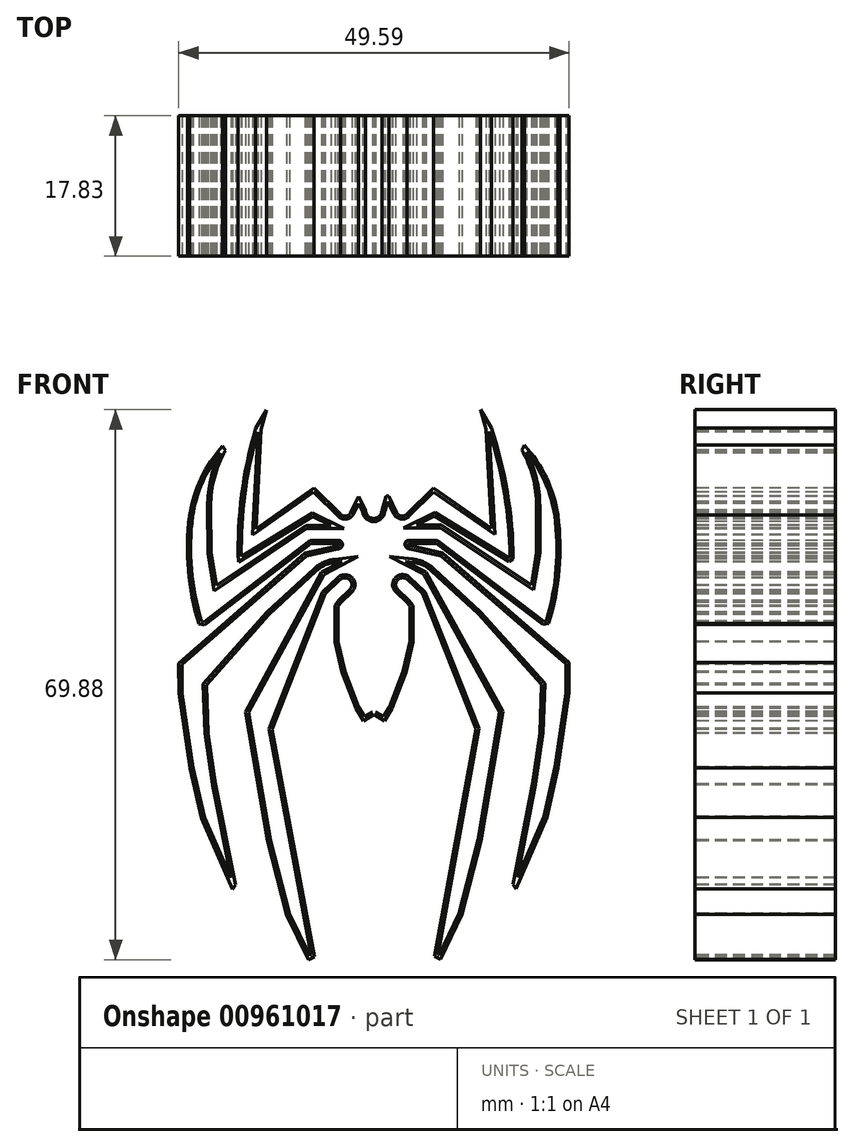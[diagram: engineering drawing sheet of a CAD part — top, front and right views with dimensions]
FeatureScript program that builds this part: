
annotation { "Feature Type Name" : "Feature", "Feature Type Description" : "" }
export const myFeature = defineFeature(function(context is Context, id is Id, definition is map)
    precondition{}
    {
        {
            var Q0;
            Q0=qCreatedBy(makeId("Front.planeOp"),FACE);
            var sketch = newSketch(context, id + "F0", { "sketchPlane" : qUnion([Q0])});
            skArc(sketch, "E0", {"start": v(10.3, 43.39) * mm, "mid": v(11.32, 42.32) * mm, "end": v(12.36, 43.36) * mm});
            skLineSegment(sketch, "E1", {"start": v(12.36, 43.36) * mm, "end": v(12.91, 45.08) * mm});
            skLineSegment(sketch, "E2", {"start": v(10.3, 43.39) * mm, "end": v(9.41, 45.08) * mm});
            skArc(sketch, "E3", {"start": v(13.25, 45.08) * mm, "mid": v(13.08, 45.2) * mm, "end": v(12.91, 45.08) * mm});
            skLineSegment(sketch, "E4", {"start": v(13.25, 45.08) * mm, "end": v(14.26, 43.06) * mm});
            skArc(sketch, "E5", {"start": v(14.26, 43.06) * mm, "mid": v(14.86, 42.62) * mm, "end": v(15.56, 42.87) * mm});
            skLineSegment(sketch, "E6", {"start": v(15.56, 42.87) * mm, "end": v(18.91, 46.2) * mm});
            skLineSegment(sketch, "E7", {"start": v(18.91, 46.2) * mm, "end": v(26.28, 41.06) * mm});
            skLineSegment(sketch, "E8", {"start": v(26.28, 41.06) * mm, "end": v(25.6, 53.69) * mm});
            skLineSegment(sketch, "E9", {"start": v(25.6, 53.69) * mm, "end": v(24.88, 56.14) * mm});
            skLineSegment(sketch, "E10", {"start": v(24.88, 56.14) * mm, "end": v(26.28, 53.79) * mm});
            skArc(sketch, "E11", {"start": v(29.06, 37.18) * mm, "mid": v(28.32, 45.6) * mm, "end": v(26.28, 53.79) * mm});
            skLineSegment(sketch, "E12", {"start": v(29.06, 37.18) * mm, "end": v(28.54, 36.84) * mm});
            skLineSegment(sketch, "E13", {"start": v(28.54, 36.84) * mm, "end": v(19.08, 42.61) * mm});
            skLineSegment(sketch, "E14", {"start": v(19.08, 42.61) * mm, "end": v(16.77, 41.46) * mm});
            skLineSegment(sketch, "E15", {"start": v(16.77, 41.46) * mm, "end": v(19.96, 41.46) * mm});
            skLineSegment(sketch, "E16", {"start": v(19.96, 41.46) * mm, "end": v(31.36, 33.86) * mm});
            skLineSegment(sketch, "E17", {"start": v(31.36, 33.86) * mm, "end": v(32.04, 38) * mm});
            skLineSegment(sketch, "E18", {"start": v(32.04, 38) * mm, "end": v(32.04, 43.9) * mm});
            skArc(sketch, "E19", {"start": v(32.04, 43.9) * mm, "mid": v(31.55, 47.6) * mm, "end": v(30.14, 51.03) * mm});
            skLineSegment(sketch, "E20", {"start": v(30.14, 51.03) * mm, "end": v(30.48, 51.61) * mm});
            skArc(sketch, "E21", {"start": v(34.72, 42.74) * mm, "mid": v(33.26, 47.5) * mm, "end": v(30.48, 51.61) * mm});
            skArc(sketch, "E22", {"start": v(33.56, 29) * mm, "mid": v(34.89, 35.8) * mm, "end": v(34.72, 42.74) * mm});
            skLineSegment(sketch, "E23", {"start": v(33.56, 29) * mm, "end": v(32.85, 28.84) * mm});
            skLineSegment(sketch, "E24", {"start": v(32.85, 28.84) * mm, "end": v(19.33, 39.16) * mm});
            skLineSegment(sketch, "E25", {"start": v(19.33, 39.16) * mm, "end": v(15.77, 39.16) * mm});
            skArc(sketch, "E26", {"start": v(15.77, 39.16) * mm, "mid": v(15.73, 38.94) * mm, "end": v(15.94, 38.86) * mm});
            skLineSegment(sketch, "E27", {"start": v(15.94, 38.86) * mm, "end": v(20.06, 37.93) * mm});
            skLineSegment(sketch, "E28", {"start": v(20.06, 37.93) * mm, "end": v(36.16, 24.01) * mm});
            skLineSegment(sketch, "E29", {"start": v(36.16, 24.01) * mm, "end": v(36.16, 20.15) * mm});
            skLineSegment(sketch, "E30", {"start": v(36.16, 20.15) * mm, "end": v(34.77, 10.65) * mm});
            skLineSegment(sketch, "E31", {"start": v(34.77, 10.65) * mm, "end": v(33.34, 4.32) * mm});
            skLineSegment(sketch, "E32", {"start": v(33.34, 4.32) * mm, "end": v(29.4, -4.75) * mm});
            skLineSegment(sketch, "E33", {"start": v(29.4, -4.75) * mm, "end": v(29.05, -4.2) * mm});
            skLineSegment(sketch, "E34", {"start": v(29.05, -4.2) * mm, "end": v(31.52, 8.6) * mm});
            skLineSegment(sketch, "E35", {"start": v(31.52, 8.6) * mm, "end": v(32.48, 15.1) * mm});
            skLineSegment(sketch, "E36", {"start": v(32.48, 15.1) * mm, "end": v(32.67, 21.21) * mm});
            skLineSegment(sketch, "E37", {"start": v(32.67, 21.21) * mm, "end": v(24.64, 30.19) * mm});
            skLineSegment(sketch, "E38", {"start": v(24.64, 30.19) * mm, "end": v(18.7, 35.66) * mm});
            skArc(sketch, "E39", {"start": v(18.7, 35.66) * mm, "mid": v(17.59, 36.4) * mm, "end": v(16.31, 36.75) * mm});
            skLineSegment(sketch, "E40", {"start": v(16.31, 36.75) * mm, "end": v(15.4, 36.86) * mm});
            skLineSegment(sketch, "E41", {"start": v(15.4, 36.86) * mm, "end": v(17.97, 35.54) * mm});
            skLineSegment(sketch, "E42", {"start": v(17.97, 35.54) * mm, "end": v(27.73, 17.79) * mm});
            skLineSegment(sketch, "E43", {"start": v(27.73, 17.79) * mm, "end": v(24.98, 1.38) * mm});
            skLineSegment(sketch, "E44", {"start": v(24.98, 1.38) * mm, "end": v(22.56, -7.98) * mm});
            skLineSegment(sketch, "E45", {"start": v(22.56, -7.98) * mm, "end": v(19.82, -13.7) * mm});
            skLineSegment(sketch, "E46", {"start": v(19.82, -13.7) * mm, "end": v(19.04, -13.34) * mm});
            skLineSegment(sketch, "E47", {"start": v(19.04, -13.34) * mm, "end": v(24.33, 15.59) * mm});
            skLineSegment(sketch, "E48", {"start": v(24.33, 15.59) * mm, "end": v(17.56, 32.78) * mm});
            skLineSegment(sketch, "E49", {"start": v(17.56, 32.78) * mm, "end": v(15.62, 34.56) * mm});
            skArc(sketch, "E50", {"start": v(15.62, 34.56) * mm, "mid": v(14.37, 34.51) * mm, "end": v(14.4, 33.26) * mm});
            skLineSegment(sketch, "E51", {"start": v(14.4, 33.26) * mm, "end": v(15.83, 31.92) * mm});
            skLineSegment(sketch, "E52", {"start": v(15.83, 31.92) * mm, "end": v(16.3, 31.27) * mm});
            skLineSegment(sketch, "E53", {"start": v(16.3, 31.27) * mm, "end": v(16.3, 26.63) * mm});
            skLineSegment(sketch, "E54", {"start": v(16.3, 26.63) * mm, "end": v(15.44, 22.78) * mm});
            skLineSegment(sketch, "E55", {"start": v(15.44, 22.78) * mm, "end": v(13.67, 18.2) * mm});
            skLineSegment(sketch, "E56", {"start": v(13.67, 18.2) * mm, "end": v(12.73, 16.61) * mm});
            skLineSegment(sketch, "E57", {"start": v(12.73, 16.61) * mm, "end": v(11.38, 17.4) * mm});
            skLineSegment(sketch, "E58.MirrorCS", {"start": v(9.41, 45.08) * mm, "end": v(8.4, 43.05) * mm});
            skArc(sketch, "E59.MirrorCS", {"start": v(8.4, 43.05) * mm, "mid": v(7.8, 42.61) * mm, "end": v(7.11, 42.86) * mm});
            skLineSegment(sketch, "E60.MirrorCS", {"start": v(7.11, 42.86) * mm, "end": v(3.74, 46.16) * mm});
            skLineSegment(sketch, "E61.MirrorCS", {"start": v(3.74, 46.16) * mm, "end": v(-3.6, 41) * mm});
            skLineSegment(sketch, "E62.MirrorCS", {"start": v(-3.6, 41) * mm, "end": v(-2.97, 53.64) * mm});
            skLineSegment(sketch, "E63.MirrorCS", {"start": v(-2.97, 53.64) * mm, "end": v(-2.26, 56.09) * mm});
            skLineSegment(sketch, "E64.MirrorCS", {"start": v(-2.26, 56.09) * mm, "end": v(-3.65, 53.73) * mm});
            skArc(sketch, "E65.MirrorCS", {"start": v(-5.85, 36.78) * mm, "mid": v(-5.43, 45.34) * mm, "end": v(-3.65, 53.73) * mm});
            skLineSegment(sketch, "E66.MirrorCS", {"start": v(-5.85, 36.78) * mm, "end": v(3.6, 42.59) * mm});
            skLineSegment(sketch, "E67.MirrorCS", {"start": v(3.6, 42.59) * mm, "end": v(5.9, 41.44) * mm});
            skLineSegment(sketch, "E68.MirrorCS", {"start": v(5.9, 41.44) * mm, "end": v(2.71, 41.43) * mm});
            skLineSegment(sketch, "E69.MirrorCS", {"start": v(2.71, 41.43) * mm, "end": v(-8.66, 33.79) * mm});
            skLineSegment(sketch, "E70.MirrorCS", {"start": v(-8.66, 33.79) * mm, "end": v(-9.35, 37.93) * mm});
            skLineSegment(sketch, "E71.MirrorCS", {"start": v(-9.35, 37.93) * mm, "end": v(-9.38, 43.83) * mm});
            skArc(sketch, "E72.MirrorCS", {"start": v(-9.38, 43.83) * mm, "mid": v(-8.9, 47.52) * mm, "end": v(-7.5, 50.96) * mm});
            skLineSegment(sketch, "E73.MirrorCS", {"start": v(-7.5, 50.96) * mm, "end": v(-7.85, 51.55) * mm});
            skArc(sketch, "E74.MirrorCS", {"start": v(-12.05, 42.65) * mm, "mid": v(-10.61, 47.41) * mm, "end": v(-7.85, 51.55) * mm});
            skArc(sketch, "E75.MirrorCS", {"start": v(-10.85, 28.92) * mm, "mid": v(-12.2, 35.72) * mm, "end": v(-12.05, 42.65) * mm});
            skLineSegment(sketch, "E76.MirrorCS", {"start": v(-10.85, 28.92) * mm, "end": v(-10.13, 28.77) * mm});
            skLineSegment(sketch, "E77.MirrorCS", {"start": v(-10.13, 28.77) * mm, "end": v(3.35, 39.13) * mm});
            skLineSegment(sketch, "E78.MirrorCS", {"start": v(3.35, 39.13) * mm, "end": v(6.91, 39.14) * mm});
            skArc(sketch, "E79.MirrorCS", {"start": v(6.91, 39.14) * mm, "mid": v(6.95, 38.92) * mm, "end": v(6.74, 38.85) * mm});
            skLineSegment(sketch, "E80.MirrorCS", {"start": v(6.74, 38.85) * mm, "end": v(2.62, 37.9) * mm});
            skLineSegment(sketch, "E81.MirrorCS", {"start": v(2.62, 37.9) * mm, "end": v(-13.43, 23.92) * mm});
            skLineSegment(sketch, "E82.MirrorCS", {"start": v(-13.43, 23.92) * mm, "end": v(-13.41, 20.06) * mm});
            skLineSegment(sketch, "E83.MirrorCS", {"start": v(-13.41, 20.06) * mm, "end": v(-11.99, 10.57) * mm});
            skLineSegment(sketch, "E84.MirrorCS", {"start": v(-11.99, 10.57) * mm, "end": v(-10.54, 4.24) * mm});
            skLineSegment(sketch, "E85.MirrorCS", {"start": v(-10.54, 4.24) * mm, "end": v(-6.57, -4.82) * mm});
            skLineSegment(sketch, "E86.MirrorCS", {"start": v(-6.57, -4.82) * mm, "end": v(-6.22, -4.26) * mm});
            skLineSegment(sketch, "E87.MirrorCS", {"start": v(-6.22, -4.26) * mm, "end": v(-8.73, 8.52) * mm});
            skLineSegment(sketch, "E88.MirrorCS", {"start": v(-8.73, 8.52) * mm, "end": v(-9.72, 15.02) * mm});
            skLineSegment(sketch, "E89.MirrorCS", {"start": v(-9.72, 15.02) * mm, "end": v(-9.93, 21.14) * mm});
            skLineSegment(sketch, "E90.MirrorCS", {"start": v(-9.93, 21.14) * mm, "end": v(-1.93, 30.14) * mm});
            skLineSegment(sketch, "E91.MirrorCS", {"start": v(-1.93, 30.14) * mm, "end": v(4, 35.64) * mm});
            skArc(sketch, "E92.MirrorCS", {"start": v(4, 35.64) * mm, "mid": v(5.1, 36.38) * mm, "end": v(6.37, 36.74) * mm});
            skLineSegment(sketch, "E93.MirrorCS", {"start": v(6.37, 36.74) * mm, "end": v(7.3, 36.84) * mm});
            skLineSegment(sketch, "E94.MirrorCS", {"start": v(7.3, 36.84) * mm, "end": v(4.72, 35.52) * mm});
            skLineSegment(sketch, "E95.MirrorCS", {"start": v(4.72, 35.52) * mm, "end": v(-4.98, 17.73) * mm});
            skLineSegment(sketch, "E96.MirrorCS", {"start": v(-4.98, 17.73) * mm, "end": v(-2.17, 1.33) * mm});
            skLineSegment(sketch, "E97.MirrorCS", {"start": v(-2.17, 1.33) * mm, "end": v(0.29, -8.02) * mm});
            skLineSegment(sketch, "E98.MirrorCS", {"start": v(0.29, -8.02) * mm, "end": v(3.05, -13.74) * mm});
            skLineSegment(sketch, "E99.MirrorCS", {"start": v(3.05, -13.74) * mm, "end": v(3.83, -13.37) * mm});
            skLineSegment(sketch, "E100.MirrorCS", {"start": v(3.83, -13.37) * mm, "end": v(-1.57, 15.54) * mm});
            skLineSegment(sketch, "E101.MirrorCS", {"start": v(-1.57, 15.54) * mm, "end": v(5.15, 32.75) * mm});
            skLineSegment(sketch, "E102.MirrorCS", {"start": v(5.15, 32.75) * mm, "end": v(7.08, 34.54) * mm});
            skArc(sketch, "E103.MirrorCS", {"start": v(7.08, 34.54) * mm, "mid": v(8.33, 34.5) * mm, "end": v(8.3, 33.25) * mm});
            skLineSegment(sketch, "E104.MirrorCS", {"start": v(8.3, 33.25) * mm, "end": v(6.87, 31.9) * mm});
            skLineSegment(sketch, "E105.MirrorCS", {"start": v(6.87, 31.9) * mm, "end": v(6.4, 31.25) * mm});
            skLineSegment(sketch, "E106.MirrorCS", {"start": v(6.4, 31.25) * mm, "end": v(6.42, 26.6) * mm});
            skLineSegment(sketch, "E107.MirrorCS", {"start": v(6.42, 26.6) * mm, "end": v(7.3, 22.76) * mm});
            skLineSegment(sketch, "E108.MirrorCS", {"start": v(7.3, 22.76) * mm, "end": v(9.08, 18.2) * mm});
            skLineSegment(sketch, "E109.MirrorCS", {"start": v(9.08, 18.2) * mm, "end": v(10.03, 16.6) * mm});
            skLineSegment(sketch, "E110.MirrorCS", {"start": v(10.03, 16.6) * mm, "end": v(11.37, 17.4) * mm});
            skLineSegment(sketch, "E111.0", {"start": v(12.6, 17.14) * mm, "end": v(11.58, 17.74) * mm});
            skLineSegment(sketch, "E111.1", {"start": v(13.32, 18.38) * mm, "end": v(12.6, 17.14) * mm});
            skLineSegment(sketch, "E111.2", {"start": v(15.07, 22.89) * mm, "end": v(13.32, 18.38) * mm});
            skLineSegment(sketch, "E111.3", {"start": v(15.92, 26.67) * mm, "end": v(15.07, 22.89) * mm});
            skLineSegment(sketch, "E111.4", {"start": v(15.92, 31.14) * mm, "end": v(15.92, 26.67) * mm});
            skLineSegment(sketch, "E111.5", {"start": v(15.54, 31.66) * mm, "end": v(15.92, 31.14) * mm});
            skLineSegment(sketch, "E111.6", {"start": v(3.7, 45.66) * mm, "end": v(-4.03, 40.23) * mm});
            skLineSegment(sketch, "E111.7", {"start": v(-4.03, 40.23) * mm, "end": v(-3.38, 53.3) * mm});
            skArc(sketch, "E111.8", {"start": v(-5.48, 37.46) * mm, "mid": v(-5.02, 45.46) * mm, "end": v(-3.38, 53.3) * mm});
            skLineSegment(sketch, "E111.9", {"start": v(-5.48, 37.46) * mm, "end": v(3.57, 43.03) * mm});
            skLineSegment(sketch, "E111.10", {"start": v(3.57, 43.03) * mm, "end": v(7.54, 41.06) * mm});
            skLineSegment(sketch, "E111.11", {"start": v(7.54, 41.06) * mm, "end": v(2.83, 41.04) * mm});
            skLineSegment(sketch, "E111.12", {"start": v(2.83, 41.04) * mm, "end": v(-8.94, 33.13) * mm});
            skLineSegment(sketch, "E111.13", {"start": v(-8.94, 33.13) * mm, "end": v(-9.74, 37.9) * mm});
            skLineSegment(sketch, "E111.14", {"start": v(-9.74, 37.9) * mm, "end": v(-9.76, 43.83) * mm});
            skArc(sketch, "E111.15", {"start": v(-9.76, 43.83) * mm, "mid": v(-9.35, 47.34) * mm, "end": v(-8.1, 50.66) * mm});
            skArc(sketch, "E111.16", {"start": v(-11.67, 42.6) * mm, "mid": v(-10.43, 46.87) * mm, "end": v(-8.1, 50.66) * mm});
            skArc(sketch, "E111.17", {"start": v(-10.55, 29.25) * mm, "mid": v(-11.82, 35.86) * mm, "end": v(-11.67, 42.6) * mm});
            skLineSegment(sketch, "E111.18", {"start": v(-10.55, 29.25) * mm, "end": v(-10.23, 29.18) * mm});
            skLineSegment(sketch, "E111.19", {"start": v(-10.23, 29.18) * mm, "end": v(3.22, 39.52) * mm});
            skLineSegment(sketch, "E111.20", {"start": v(3.22, 39.52) * mm, "end": v(7, 39.53) * mm});
            skArc(sketch, "E111.21", {"start": v(7, 39.53) * mm, "mid": v(7.35, 38.88) * mm, "end": v(6.75, 38.45) * mm});
            skLineSegment(sketch, "E111.22", {"start": v(6.75, 38.45) * mm, "end": v(2.8, 37.55) * mm});
            skLineSegment(sketch, "E111.23", {"start": v(2.8, 37.55) * mm, "end": v(-13.04, 23.75) * mm});
            skLineSegment(sketch, "E111.24", {"start": v(-13.04, 23.75) * mm, "end": v(-13.03, 20.1) * mm});
            skLineSegment(sketch, "E111.25", {"start": v(-13.03, 20.1) * mm, "end": v(-11.6, 10.64) * mm});
            skLineSegment(sketch, "E111.26", {"start": v(-11.6, 10.64) * mm, "end": v(-10.17, 4.36) * mm});
            skLineSegment(sketch, "E111.27", {"start": v(-10.17, 4.36) * mm, "end": v(-6.79, -3.36) * mm});
            skLineSegment(sketch, "E111.28", {"start": v(-6.79, -3.36) * mm, "end": v(-9.11, 8.45) * mm});
            skLineSegment(sketch, "E111.29", {"start": v(-9.11, 8.45) * mm, "end": v(-10.1, 14.98) * mm});
            skLineSegment(sketch, "E111.30", {"start": v(-1.97, 15.58) * mm, "end": v(4.82, 32.98) * mm});
            skLineSegment(sketch, "E111.31", {"start": v(4.82, 32.98) * mm, "end": v(6.81, 34.83) * mm});
            skArc(sketch, "E111.32", {"start": v(6.81, 34.83) * mm, "mid": v(8.6, 34.76) * mm, "end": v(8.56, 32.97) * mm});
            skLineSegment(sketch, "E111.33", {"start": v(8.56, 32.97) * mm, "end": v(7.17, 31.64) * mm});
            skLineSegment(sketch, "E111.34", {"start": v(7.17, 31.64) * mm, "end": v(6.8, 31.13) * mm});
            skLineSegment(sketch, "E111.35", {"start": v(6.8, 31.13) * mm, "end": v(6.8, 26.65) * mm});
            skLineSegment(sketch, "E111.36", {"start": v(10.16, 17.14) * mm, "end": v(11.17, 17.74) * mm});
            skLineSegment(sketch, "E111.37", {"start": v(9.43, 18.37) * mm, "end": v(10.16, 17.14) * mm});
            skLineSegment(sketch, "E111.38", {"start": v(7.67, 22.87) * mm, "end": v(9.43, 18.37) * mm});
            skLineSegment(sketch, "E111.39", {"start": v(6.8, 26.65) * mm, "end": v(7.67, 22.87) * mm});
            skLineSegment(sketch, "E111.40", {"start": v(3.4, -13.15) * mm, "end": v(-1.97, 15.58) * mm});
            skLineSegment(sketch, "E111.41", {"start": v(3.23, -13.22) * mm, "end": v(3.4, -13.15) * mm});
            skLineSegment(sketch, "E111.42", {"start": v(0.65, -7.88) * mm, "end": v(3.23, -13.22) * mm});
            skLineSegment(sketch, "E111.43", {"start": v(-1.79, 1.42) * mm, "end": v(0.65, -7.88) * mm});
            skLineSegment(sketch, "E111.44", {"start": v(-4.57, 17.66) * mm, "end": v(-1.79, 1.42) * mm});
            skLineSegment(sketch, "E111.45", {"start": v(5, 35.23) * mm, "end": v(-4.57, 17.66) * mm});
            skLineSegment(sketch, "E111.46", {"start": v(9.36, 37.48) * mm, "end": v(5, 35.23) * mm});
            skLineSegment(sketch, "E111.47", {"start": v(6.33, 37.12) * mm, "end": v(9.36, 37.48) * mm});
            skArc(sketch, "E111.48", {"start": v(3.74, 35.92) * mm, "mid": v(4.94, 36.73) * mm, "end": v(6.33, 37.12) * mm});
            skLineSegment(sketch, "E111.49", {"start": v(-2.2, 30.41) * mm, "end": v(3.74, 35.92) * mm});
            skLineSegment(sketch, "E111.50", {"start": v(-10.32, 21.28) * mm, "end": v(-2.2, 30.41) * mm});
            skLineSegment(sketch, "E111.51", {"start": v(-10.1, 14.98) * mm, "end": v(-10.32, 21.28) * mm});
            skLineSegment(sketch, "E111.52", {"start": v(6.83, 42.59) * mm, "end": v(3.7, 45.66) * mm});
            skArc(sketch, "E111.53", {"start": v(8.75, 42.88) * mm, "mid": v(7.87, 42.23) * mm, "end": v(6.83, 42.59) * mm});
            skLineSegment(sketch, "E111.54", {"start": v(9.42, 44.23) * mm, "end": v(8.75, 42.88) * mm});
            skLineSegment(sketch, "E111.55", {"start": v(9.92, 43.29) * mm, "end": v(9.42, 44.23) * mm});
            skArc(sketch, "E111.56", {"start": v(9.92, 43.29) * mm, "mid": v(11.33, 41.93) * mm, "end": v(12.75, 43.3) * mm});
            skLineSegment(sketch, "E111.57", {"start": v(12.75, 43.3) * mm, "end": v(13.12, 44.46) * mm});
            skLineSegment(sketch, "E111.58", {"start": v(13.12, 44.46) * mm, "end": v(13.91, 42.88) * mm});
            skArc(sketch, "E111.59", {"start": v(13.91, 42.88) * mm, "mid": v(14.8, 42.24) * mm, "end": v(15.83, 42.6) * mm});
            skLineSegment(sketch, "E111.60", {"start": v(15.83, 42.6) * mm, "end": v(18.96, 45.69) * mm});
            skLineSegment(sketch, "E111.61", {"start": v(18.96, 45.69) * mm, "end": v(26.7, 40.29) * mm});
            skLineSegment(sketch, "E111.62", {"start": v(26.7, 40.29) * mm, "end": v(26, 53.39) * mm});
            skArc(sketch, "E111.63", {"start": v(28.67, 37.39) * mm, "mid": v(27.94, 45.49) * mm, "end": v(26, 53.39) * mm});
            skLineSegment(sketch, "E111.64", {"start": v(28.67, 37.39) * mm, "end": v(28.53, 37.3) * mm});
            skLineSegment(sketch, "E111.65", {"start": v(28.53, 37.3) * mm, "end": v(19.1, 43.06) * mm});
            skLineSegment(sketch, "E111.66", {"start": v(19.1, 43.06) * mm, "end": v(15.13, 41.07) * mm});
            skLineSegment(sketch, "E111.67", {"start": v(15.13, 41.07) * mm, "end": v(19.84, 41.07) * mm});
            skLineSegment(sketch, "E111.68", {"start": v(19.84, 41.07) * mm, "end": v(31.64, 33.2) * mm});
            skLineSegment(sketch, "E111.69", {"start": v(31.64, 33.2) * mm, "end": v(32.42, 37.97) * mm});
            skLineSegment(sketch, "E111.70", {"start": v(32.42, 37.97) * mm, "end": v(32.42, 43.9) * mm});
            skArc(sketch, "E111.71", {"start": v(32.42, 43.9) * mm, "mid": v(32, 47.42) * mm, "end": v(30.74, 50.73) * mm});
            skArc(sketch, "E111.72", {"start": v(34.34, 42.68) * mm, "mid": v(33.09, 46.95) * mm, "end": v(30.74, 50.73) * mm});
            skArc(sketch, "E111.73", {"start": v(33.26, 29.33) * mm, "mid": v(34.51, 35.95) * mm, "end": v(34.34, 42.68) * mm});
            skLineSegment(sketch, "E111.74", {"start": v(33.26, 29.33) * mm, "end": v(32.94, 29.26) * mm});
            skLineSegment(sketch, "E111.75", {"start": v(32.94, 29.26) * mm, "end": v(19.46, 39.54) * mm});
            skLineSegment(sketch, "E111.76", {"start": v(19.46, 39.54) * mm, "end": v(15.67, 39.54) * mm});
            skArc(sketch, "E111.77", {"start": v(15.67, 39.54) * mm, "mid": v(15.33, 38.89) * mm, "end": v(15.94, 38.47) * mm});
            skLineSegment(sketch, "E111.78", {"start": v(15.94, 38.47) * mm, "end": v(19.88, 37.58) * mm});
            skLineSegment(sketch, "E111.79", {"start": v(19.88, 37.58) * mm, "end": v(35.77, 23.83) * mm});
            skLineSegment(sketch, "E111.80", {"start": v(35.77, 23.83) * mm, "end": v(35.77, 20.18) * mm});
            skLineSegment(sketch, "E111.81", {"start": v(35.77, 20.18) * mm, "end": v(34.39, 10.72) * mm});
            skLineSegment(sketch, "E111.82", {"start": v(34.39, 10.72) * mm, "end": v(32.97, 4.44) * mm});
            skLineSegment(sketch, "E111.83", {"start": v(32.97, 4.44) * mm, "end": v(29.62, -3.3) * mm});
            skLineSegment(sketch, "E111.84", {"start": v(29.62, -3.3) * mm, "end": v(31.9, 8.53) * mm});
            skLineSegment(sketch, "E111.85", {"start": v(31.9, 8.53) * mm, "end": v(32.87, 15.06) * mm});
            skLineSegment(sketch, "E111.86", {"start": v(32.87, 15.06) * mm, "end": v(33.07, 21.36) * mm});
            skLineSegment(sketch, "E111.87", {"start": v(33.07, 21.36) * mm, "end": v(24.92, 30.46) * mm});
            skLineSegment(sketch, "E111.88", {"start": v(24.92, 30.46) * mm, "end": v(18.96, 35.95) * mm});
            skArc(sketch, "E111.89", {"start": v(18.96, 35.95) * mm, "mid": v(17.75, 36.75) * mm, "end": v(16.36, 37.14) * mm});
            skLineSegment(sketch, "E111.90", {"start": v(16.36, 37.14) * mm, "end": v(13.32, 37.49) * mm});
            skLineSegment(sketch, "E111.91", {"start": v(13.32, 37.49) * mm, "end": v(17.69, 35.25) * mm});
            skLineSegment(sketch, "E111.92", {"start": v(17.69, 35.25) * mm, "end": v(27.33, 17.72) * mm});
            skLineSegment(sketch, "E111.93", {"start": v(27.33, 17.72) * mm, "end": v(24.6, 1.46) * mm});
            skLineSegment(sketch, "E111.94", {"start": v(24.6, 1.46) * mm, "end": v(22.2, -7.85) * mm});
            skLineSegment(sketch, "E111.95", {"start": v(22.2, -7.85) * mm, "end": v(19.63, -13.2) * mm});
            skLineSegment(sketch, "E111.96", {"start": v(19.63, -13.2) * mm, "end": v(19.47, -13.12) * mm});
            skLineSegment(sketch, "E111.97", {"start": v(19.47, -13.12) * mm, "end": v(24.73, 15.62) * mm});
            skLineSegment(sketch, "E111.98", {"start": v(24.73, 15.62) * mm, "end": v(17.88, 33) * mm});
            skLineSegment(sketch, "E111.99", {"start": v(17.88, 33) * mm, "end": v(15.88, 34.84) * mm});
            skArc(sketch, "E111.100", {"start": v(15.88, 34.84) * mm, "mid": v(14.09, 34.77) * mm, "end": v(14.14, 32.98) * mm});
            skLineSegment(sketch, "E111.101", {"start": v(14.14, 32.98) * mm, "end": v(15.54, 31.66) * mm});
            skSolve(sketch);
        }
        {
            var Q0;
            Q0=qSketchRegion(id+"F0",true);
            var Q1;
            Q1=sQuery(id+"F0.wireOp",EDGE,"E111.72");
            var Q2;
            Q2=sQuery(id+"F0.wireOp",EDGE,"E21");
            var Q3;
            Q3=sQuery(id+"F0.wireOp",EDGE,"E111.73");
            var Q4;
            Q4=sQuery(id+"F0.wireOp",EDGE,"E22");
            var Q5;
            Q5=sQuery(id+"F0.wireOp",EDGE,"E111.71");
            var Q6;
            Q6=sQuery(id+"F0.wireOp",EDGE,"E20");
            var Q7;
            Q7=sQuery(id+"F0.wireOp",EDGE,"E111.45");
            var Q8;
            Q8=sQuery(id+"F0.wireOp",EDGE,"E111.93");
            var Q9;
            Q9=sQuery(id+"F0.wireOp",EDGE,"E53");
            var Q10;
            Q10=sQuery(id+"F0.wireOp",EDGE,"E111.6");
            var Q11;
            Q11=sQuery(id+"F0.wireOp",EDGE,"E81.MirrorCS");
            var Q12;
            Q12=sQuery(id+"F0.wireOp",EDGE,"E111.2");
            var Q13;
            Q13=sQuery(id+"F0.wireOp",EDGE,"E17");
            var Q14;
            Q14=sQuery(id+"F0.wireOp",EDGE,"E111.30");
            var Q15;
            Q15=sQuery(id+"F0.wireOp",EDGE,"E111.69");
            var Q16;
            Q16=sQuery(id+"F0.wireOp",EDGE,"E29");
            var Q17;
            Q17=sQuery(id+"F0.wireOp",EDGE,"E111.13");
            var Q18;
            Q18=sQuery(id+"F0.wireOp",EDGE,"E111.98");
            var Q19;
            Q19=sQuery(id+"F0.wireOp",EDGE,"E111.94");
            var Q20;
            Q20=sQuery(id+"F0.wireOp",EDGE,"E37");
            var Q21;
            Q21=sQuery(id+"F0.wireOp",EDGE,"E111.25");
            var Q22;
            Q22=sQuery(id+"F0.wireOp",EDGE,"E24");
            var Q23;
            Q23=sQuery(id+"F0.wireOp",EDGE,"E111.50");
            var Q24;
            Q24=sQuery(id+"F0.wireOp",EDGE,"E111.38");
            var Q25;
            Q25=sQuery(id+"F0.wireOp",EDGE,"E97.MirrorCS");
            var Q26;
            Q26=sQuery(id+"F0.wireOp",EDGE,"E16");
            var Q27;
            Q27=sQuery(id+"F0.wireOp",EDGE,"E48");
            var Q28;
            Q28=sQuery(id+"F0.wireOp",EDGE,"E85.MirrorCS");
            var Q29;
            Q29=sQuery(id+"F0.wireOp",EDGE,"E32");
            var Q30;
            Q30=sQuery(id+"F0.wireOp",EDGE,"E111.63");
            var Q31;
            Q31=sQuery(id+"F0.wireOp",EDGE,"E108.MirrorCS");
            var Q32;
            Q32=sQuery(id+"F0.wireOp",EDGE,"E111.14");
            var Q33;
            Q33=sQuery(id+"F0.wireOp",EDGE,"E111.29");
            var Q34;
            Q34=sQuery(id+"F0.wireOp",EDGE,"E111.62");
            var Q35;
            Q35=sQuery(id+"F0.wireOp",EDGE,"E65.MirrorCS");
            var Q36;
            Q36=sQuery(id+"F0.wireOp",EDGE,"E44");
            var Q37;
            Q37=sQuery(id+"F0.wireOp",EDGE,"E96.MirrorCS");
            var Q38;
            Q38=sQuery(id+"F0.wireOp",EDGE,"E111.15");
            var Q39;
            Q39=sQuery(id+"F0.wireOp",EDGE,"E55");
            var Q40;
            Q40=sQuery(id+"F0.wireOp",EDGE,"E88.MirrorCS");
            var Q41;
            Q41=sQuery(id+"F0.wireOp",EDGE,"E72.MirrorCS");
            var Q42;
            Q42=sQuery(id+"F0.wireOp",EDGE,"E111.85");
            var Q43;
            Q43=sQuery(id+"F0.wireOp",EDGE,"E61.MirrorCS");
            var Q44;
            Q44=sQuery(id+"F0.wireOp",EDGE,"E77.MirrorCS");
            var Q45;
            Q45=sQuery(id+"F0.wireOp",EDGE,"E111.8");
            var Q46;
            Q46=sQuery(id+"F0.wireOp",EDGE,"E101.MirrorCS");
            var Q47;
            Q47=sQuery(id+"F0.wireOp",EDGE,"E111.24");
            var Q48;
            Q48=sQuery(id+"F0.wireOp",EDGE,"E111.95");
            var Q49;
            Q49=sQuery(id+"F0.wireOp",EDGE,"E111.82");
            var Q50;
            Q50=sQuery(id+"F0.wireOp",EDGE,"E28");
            var Q51;
            Q51=sQuery(id+"F0.wireOp",EDGE,"E62.MirrorCS");
            var Q52;
            Q52=sQuery(id+"F0.wireOp",EDGE,"E69.MirrorCS");
            var Q53;
            Q53=sQuery(id+"F0.wireOp",EDGE,"E84.MirrorCS");
            var Q54;
            Q54=sQuery(id+"F0.wireOp",EDGE,"E45");
            var Q55;
            Q55=sQuery(id+"F0.wireOp",EDGE,"E111.88");
            var Q56;
            Q56=sQuery(id+"F0.wireOp",EDGE,"E36");
            var Q57;
            Q57=sQuery(id+"F0.wireOp",EDGE,"E100.MirrorCS");
            var Q58;
            Q58=sQuery(id+"F0.wireOp",EDGE,"E111.79");
            var Q59;
            Q59=sQuery(id+"F0.wireOp",EDGE,"E111.86");
            var Q60;
            Q60=sQuery(id+"F0.wireOp",EDGE,"E30");
            var Q61;
            Q61=sQuery(id+"F0.wireOp",EDGE,"E111.9");
            var Q62;
            Q62=sQuery(id+"F0.wireOp",EDGE,"E111.40");
            var Q63;
            Q63=sQuery(id+"F0.wireOp",EDGE,"E111.61");
            var Q64;
            Q64=sQuery(id+"F0.wireOp",EDGE,"E111.70");
            var Q65;
            Q65=sQuery(id+"F0.wireOp",EDGE,"E11");
            var Q66;
            Q66=sQuery(id+"F0.wireOp",EDGE,"E111.23");
            var Q67;
            Q67=sQuery(id+"F0.wireOp",EDGE,"E31");
            var Q68;
            Q68=sQuery(id+"F0.wireOp",EDGE,"E35");
            var Q69;
            Q69=sQuery(id+"F0.wireOp",EDGE,"E111.26");
            var Q70;
            Q70=sQuery(id+"F0.wireOp",EDGE,"E7");
            var Q71;
            Q71=sQuery(id+"F0.wireOp",EDGE,"E95.MirrorCS");
            var Q72;
            Q72=sQuery(id+"F0.wireOp",EDGE,"E43");
            var Q73;
            Q73=sQuery(id+"F0.wireOp",EDGE,"E111.12");
            var Q74;
            Q74=sQuery(id+"F0.wireOp",EDGE,"E75.MirrorCS");
            var Q75;
            Q75=sQuery(id+"F0.wireOp",EDGE,"E111.97");
            var Q76;
            Q76=sQuery(id+"F0.wireOp",EDGE,"E89.MirrorCS");
            var Q77;
            Q77=sQuery(id+"F0.wireOp",EDGE,"E91.MirrorCS");
            var Q78;
            Q78=sQuery(id+"F0.wireOp",EDGE,"E34");
            var Q79;
            Q79=sQuery(id+"F0.wireOp",EDGE,"E18");
            var Q80;
            Q80=sQuery(id+"F0.wireOp",EDGE,"E74.MirrorCS");
            var Q81;
            Q81=sQuery(id+"F0.wireOp",EDGE,"E98.MirrorCS");
            var Q82;
            Q82=sQuery(id+"F0.wireOp",EDGE,"E47");
            var Q83;
            Q83=sQuery(id+"F0.wireOp",EDGE,"E111.16");
            var Q84;
            Q84=sQuery(id+"F0.wireOp",EDGE,"E111.68");
            var Q85;
            Q85=sQuery(id+"F0.wireOp",EDGE,"E111.75");
            var Q86;
            Q86=sQuery(id+"F0.wireOp",EDGE,"E27");
            var Q87;
            Q87=sQuery(id+"F0.wireOp",EDGE,"E54");
            var Q88;
            Q88=sQuery(id+"F0.wireOp",EDGE,"E111.28");
            var Q89;
            Q89=sQuery(id+"F0.wireOp",EDGE,"E13");
            var Q90;
            Q90=sQuery(id+"F0.wireOp",EDGE,"E111.44");
            var Q91;
            Q91=sQuery(id+"F0.wireOp",EDGE,"E111.81");
            var Q92;
            Q92=sQuery(id+"F0.wireOp",EDGE,"E111.3");
            var Q93;
            Q93=sQuery(id+"F0.wireOp",EDGE,"E111.83");
            var Q94;
            Q94=sQuery(id+"F0.wireOp",EDGE,"E111.35");
            var Q95;
            Q95=sQuery(id+"F0.wireOp",EDGE,"E111.7");
            var Q96;
            Q96=sQuery(id+"F0.wireOp",EDGE,"E111.87");
            var Q97;
            Q97=sQuery(id+"F0.wireOp",EDGE,"E111.17");
            var Q98;
            Q98=sQuery(id+"F0.wireOp",EDGE,"E106.MirrorCS");
            var Q99;
            Q99=sQuery(id+"F0.wireOp",EDGE,"E19");
            var Q100;
            Q100=sQuery(id+"F0.wireOp",EDGE,"E70.MirrorCS");
            var Q101;
            Q101=sQuery(id+"F0.wireOp",EDGE,"E8");
            var Q102;
            Q102=sQuery(id+"F0.wireOp",EDGE,"E111.27");
            var Q103;
            Q103=sQuery(id+"F0.wireOp",EDGE,"E83.MirrorCS");
            var Q104;
            Q104=sQuery(id+"F0.wireOp",EDGE,"E38");
            var Q105;
            Q105=sQuery(id+"F0.wireOp",EDGE,"E111.65");
            var Q106;
            Q106=sQuery(id+"F0.wireOp",EDGE,"E111.43");
            var Q107;
            Q107=sQuery(id+"F0.wireOp",EDGE,"E111.49");
            var Q108;
            Q108=sQuery(id+"F0.wireOp",EDGE,"E111.19");
            var Q109;
            Q109=sQuery(id+"F0.wireOp",EDGE,"E111.92");
            var Q110;
            Q110=sQuery(id+"F0.wireOp",EDGE,"E90.MirrorCS");
            var Q111;
            Q111=sQuery(id+"F0.wireOp",EDGE,"E111.51");
            var Q112;
            Q112=sQuery(id+"F0.wireOp",EDGE,"E42");
            var Q113;
            Q113=sQuery(id+"F0.wireOp",EDGE,"E87.MirrorCS");
            var Q114;
            Q114=sQuery(id+"F0.wireOp",EDGE,"E107.MirrorCS");
            var Q115;
            Q115=sQuery(id+"F0.wireOp",EDGE,"E111.84");
            var Q116;
            Q116=sQuery(id+"F0.wireOp",EDGE,"E111.42");
            var Q117;
            Q117=sQuery(id+"F0.wireOp",EDGE,"E66.MirrorCS");
            var Q118;
            Q118=sQuery(id+"F0.wireOp",EDGE,"E111.39");
            var Q119;
            Q119=sQuery(id+"F0.wireOp",EDGE,"E111.80");
            var Q120;
            Q120=sQuery(id+"F0.wireOp",EDGE,"E111.4");
            var Q121;
            Q121=sQuery(id+"F0.wireOp",EDGE,"E82.MirrorCS");
            var Q122;
            Q122=sQuery(id+"F0.wireOp",EDGE,"E71.MirrorCS");
            var Q123;
            Q123=sQuery(id+"F0.wireOp",EDGE,"E49");
            var Q124;
            Q124=sQuery(id+"F0.wireOp",EDGE,"E111.66");
            var Q125;
            Q125=sQuery(id+"F0.wireOp",EDGE,"E111.22");
            var Q126;
            Q126=sQuery(id+"F0.wireOp",EDGE,"E103.MirrorCS");
            var Q127;
            Q127=sQuery(id+"F0.wireOp",EDGE,"E104.MirrorCS");
            var Q128;
            Q128=sQuery(id+"F0.wireOp",EDGE,"E80.MirrorCS");
            var Q129;
            Q129=sQuery(id+"F0.wireOp",EDGE,"E111.1");
            var Q130;
            Q130=sQuery(id+"F0.wireOp",EDGE,"E111.46");
            var Q131;
            Q131=sQuery(id+"F0.wireOp",EDGE,"E60.MirrorCS");
            var Q132;
            Q132=sQuery(id+"F0.wireOp",EDGE,"E33");
            var Q133;
            Q133=sQuery(id+"F0.wireOp",EDGE,"E68.MirrorCS");
            var Q134;
            Q134=sQuery(id+"F0.wireOp",EDGE,"E64.MirrorCS");
            var Q135;
            Q135=sQuery(id+"F0.wireOp",EDGE,"E111.47");
            var Q136;
            Q136=sQuery(id+"F0.wireOp",EDGE,"E78.MirrorCS");
            var Q137;
            Q137=sQuery(id+"F0.wireOp",EDGE,"E111.37");
            var Q138;
            Q138=sQuery(id+"F0.wireOp",EDGE,"E111.20");
            var Q139;
            Q139=sQuery(id+"F0.wireOp",EDGE,"E73.MirrorCS");
            var Q140;
            Q140=sQuery(id+"F0.wireOp",EDGE,"E111.60");
            var Q141;
            Q141=sQuery(id+"F0.wireOp",EDGE,"E111.91");
            var Q142;
            Q142=sQuery(id+"F0.wireOp",EDGE,"E10");
            var Q143;
            Q143=sQuery(id+"F0.wireOp",EDGE,"E111.52");
            var Q144;
            Q144=sQuery(id+"F0.wireOp",EDGE,"E111.100");
            var Q145;
            Q145=sQuery(id+"F0.wireOp",EDGE,"E111.99");
            var Q146;
            Q146=sQuery(id+"F0.wireOp",EDGE,"E2");
            var Q147;
            Q147=sQuery(id+"F0.wireOp",EDGE,"E111.11");
            var Q148;
            Q148=sQuery(id+"F0.wireOp",EDGE,"E6");
            var Q149;
            Q149=sQuery(id+"F0.wireOp",EDGE,"E86.MirrorCS");
            var Q150;
            Q150=sQuery(id+"F0.wireOp",EDGE,"E111.76");
            var Q151;
            Q151=sQuery(id+"F0.wireOp",EDGE,"E111.10");
            var Q152;
            Q152=sQuery(id+"F0.wireOp",EDGE,"E23");
            var Q153;
            Q153=sQuery(id+"F0.wireOp",EDGE,"E111.32");
            var Q154;
            Q154=sQuery(id+"F0.wireOp",EDGE,"E111.34");
            var Q155;
            Q155=sQuery(id+"F0.wireOp",EDGE,"E111.53");
            var Q156;
            Q156=sQuery(id+"F0.wireOp",EDGE,"E111.54");
            var Q157;
            Q157=sQuery(id+"F0.wireOp",EDGE,"E56");
            var Q158;
            Q158=sQuery(id+"F0.wireOp",EDGE,"E111.31");
            var Q159;
            Q159=sQuery(id+"F0.wireOp",EDGE,"E102.MirrorCS");
            var Q160;
            Q160=sQuery(id+"F0.wireOp",EDGE,"E58.MirrorCS");
            var Q161;
            Q161=sQuery(id+"F0.wireOp",EDGE,"E25");
            var Q162;
            Q162=sQuery(id+"F0.wireOp",EDGE,"E67.MirrorCS");
            var Q163;
            Q163=sQuery(id+"F0.wireOp",EDGE,"E9");
            var Q164;
            Q164=sQuery(id+"F0.wireOp",EDGE,"E111.90");
            var Q165;
            Q165=sQuery(id+"F0.wireOp",EDGE,"E111.74");
            var Q166;
            Q166=sQuery(id+"F0.wireOp",EDGE,"E111.67");
            var Q167;
            Q167=sQuery(id+"F0.wireOp",EDGE,"E63.MirrorCS");
            var Q168;
            Q168=sQuery(id+"F0.wireOp",EDGE,"E111.33");
            var Q169;
            Q169=sQuery(id+"F0.wireOp",EDGE,"E105.MirrorCS");
            var Q170;
            Q170=sQuery(id+"F0.wireOp",EDGE,"E46");
            var Q171;
            Q171=sQuery(id+"F0.wireOp",EDGE,"E111.18");
            var Q172;
            Q172=sQuery(id+"F0.wireOp",EDGE,"E111.101");
            var Q173;
            Q173=sQuery(id+"F0.wireOp",EDGE,"E111.89");
            var Q174;
            Q174=sQuery(id+"F0.wireOp",EDGE,"E94.MirrorCS");
            var Q175;
            Q175=sQuery(id+"F0.wireOp",EDGE,"E76.MirrorCS");
            var Q176;
            Q176=sQuery(id+"F0.wireOp",EDGE,"E111.57");
            var Q177;
            Q177=sQuery(id+"F0.wireOp",EDGE,"E111.56");
            var Q178;
            Q178=sQuery(id+"F0.wireOp",EDGE,"E39");
            var Q179;
            Q179=sQuery(id+"F0.wireOp",EDGE,"E110.MirrorCS");
            var Q180;
            Q180=sQuery(id+"F0.wireOp",EDGE,"E109.MirrorCS");
            var Q181;
            Q181=sQuery(id+"F0.wireOp",EDGE,"E111.78");
            var Q182;
            Q182=sQuery(id+"F0.wireOp",EDGE,"E52");
            var Q183;
            Q183=sQuery(id+"F0.wireOp",EDGE,"E92.MirrorCS");
            var Q184;
            Q184=sQuery(id+"F0.wireOp",EDGE,"E111.41");
            var Q185;
            Q185=sQuery(id+"F0.wireOp",EDGE,"E111.5");
            var Q186;
            Q186=sQuery(id+"F0.wireOp",EDGE,"E40");
            var Q187;
            Q187=sQuery(id+"F0.wireOp",EDGE,"E111.36");
            var Q188;
            Q188=sQuery(id+"F0.wireOp",EDGE,"E41");
            var Q189;
            Q189=sQuery(id+"F0.wireOp",EDGE,"E5");
            var Q190;
            Q190=sQuery(id+"F0.wireOp",EDGE,"E12");
            var Q191;
            Q191=sQuery(id+"F0.wireOp",EDGE,"E51");
            var Q192;
            Q192=sQuery(id+"F0.wireOp",EDGE,"E59.MirrorCS");
            var Q193;
            Q193=sQuery(id+"F0.wireOp",EDGE,"E111.48");
            var Q194;
            Q194=sQuery(id+"F0.wireOp",EDGE,"E99.MirrorCS");
            var Q195;
            Q195=sQuery(id+"F0.wireOp",EDGE,"E50");
            var Q196;
            Q196=sQuery(id+"F0.wireOp",EDGE,"E111.59");
            var Q197;
            Q197=sQuery(id+"F0.wireOp",EDGE,"E15");
            var Q198;
            Q198=sQuery(id+"F0.wireOp",EDGE,"E111.96");
            var Q199;
            Q199=sQuery(id+"F0.wireOp",EDGE,"E111.58");
            var Q200;
            Q200=sQuery(id+"F0.wireOp",EDGE,"E111.0");
            var Q201;
            Q201=sQuery(id+"F0.wireOp",EDGE,"E14");
            var Q202;
            Q202=sQuery(id+"F0.wireOp",EDGE,"E0");
            var Q203;
            Q203=sQuery(id+"F0.wireOp",EDGE,"E57");
            var Q204;
            Q204=sQuery(id+"F0.wireOp",EDGE,"E93.MirrorCS");
            var Q205;
            Q205=sQuery(id+"F0.wireOp",EDGE,"E111.55");
            var Q206;
            Q206=sQuery(id+"F0.wireOp",EDGE,"E111.64");
            var Q207;
            Q207=sQuery(id+"F0.wireOp",EDGE,"E4");
            var Q208;
            Q208=sQuery(id+"F0.wireOp",EDGE,"E111.21");
            var Q209;
            Q209=sQuery(id+"F0.wireOp",EDGE,"E111.77");
            var Q210;
            Q210=sQuery(id+"F0.wireOp",EDGE,"E79.MirrorCS");
            var Q211;
            Q211=sQuery(id+"F0.wireOp",EDGE,"E26");
            var Q212;
            Q212=sQuery(id+"F0.wireOp",EDGE,"E3");
            var Q213;
            Q213=sQuery(id+"F0.wireOp",EDGE,"E1");
            extrude(context, id + "F1", {"entities" : qUnion([Q0]), "bodyType" : ToolBodyType.SURFACE, "operationType" : NewBodyOperationType.ADD, "surfaceEntities" : qUnion([Q1, Q2, Q3, Q4, Q5, Q6, Q7, Q8, Q9, Q10, Q11, Q12, Q13, Q14, Q15, Q16, Q17, Q18, Q19, Q20, Q21, Q22, Q23, Q24, Q25, Q26, Q27, Q28, Q29, Q30, Q31, Q32, Q33, Q34, Q35, Q36, Q37, Q38, Q39, Q40, Q41, Q42, Q43, Q44, Q45, Q46, Q47, Q48, Q49, Q50, Q51, Q52, Q53, Q54, Q55, Q56, Q57, Q58, Q59, Q60, Q61, Q62, Q63, Q64, Q65, Q66, Q67, Q68, Q69, Q70, Q71, Q72, Q73, Q74, Q75, Q76, Q77, Q78, Q79, Q80, Q81, Q82, Q83, Q84, Q85, Q86, Q87, Q88, Q89, Q90, Q91, Q92, Q93, Q94, Q95, Q96, Q97, Q98, Q99, Q100, Q101, Q102, Q103, Q104, Q105, Q106, Q107, Q108, Q109, Q110, Q111, Q112, Q113, Q114, Q115, Q116, Q117, Q118, Q119, Q120, Q121, Q122, Q123, Q124, Q125, Q126, Q127, Q128, Q129, Q130, Q131, Q132, Q133, Q134, Q135, Q136, Q137, Q138, Q139, Q140, Q141, Q142, Q143, Q144, Q145, Q146, Q147, Q148, Q149, Q150, Q151, Q152, Q153, Q154, Q155, Q156, Q157, Q158, Q159, Q160, Q161, Q162, Q163, Q164, Q165, Q166, Q167, Q168, Q169, Q170, Q171, Q172, Q173, Q174, Q175, Q176, Q177, Q178, Q179, Q180, Q181, Q182, Q183, Q184, Q185, Q186, Q187, Q188, Q189, Q190, Q191, Q192, Q193, Q194, Q195, Q196, Q197, Q198, Q199, Q200, Q201, Q202, Q203, Q204, Q205, Q206, Q207, Q208, Q209, Q210, Q211, Q212, Q213]), "depth" : 17.83 * mm, "offsetDistance" : 25.4 * mm});
        }
    });
